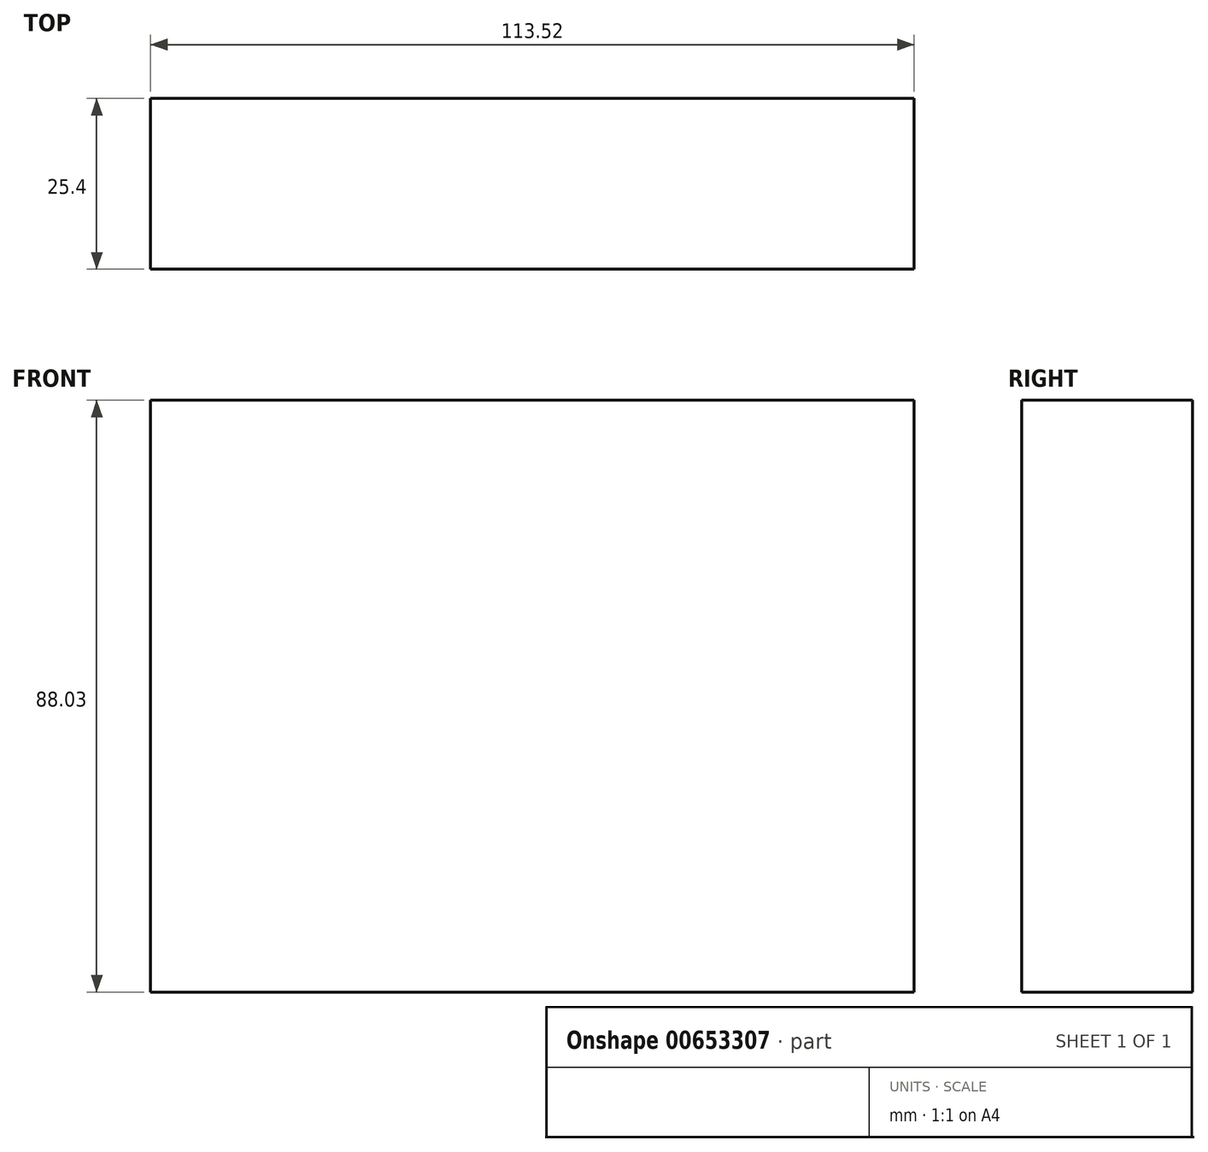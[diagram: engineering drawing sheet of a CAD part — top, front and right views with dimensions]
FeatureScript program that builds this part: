
annotation { "Feature Type Name" : "Feature", "Feature Type Description" : "" }
export const myFeature = defineFeature(function(context is Context, id is Id, definition is map)
    precondition{}
    {
        {
            var Q0;
            Q0=qCreatedBy(makeId("Front.planeOp"),FACE);
            var sketch = newSketch(context, id + "F0", { "sketchPlane" : qUnion([Q0])});
            skLineSegment(sketch, "E0.bottom", {"start": v(-50.13, 54) * mm, "end": v(63.4, 54) * mm});
            skLineSegment(sketch, "E0.top", {"start": v(-50.13, -34.04) * mm, "end": v(63.4, -34.04) * mm});
            skLineSegment(sketch, "E0.left", {"start": v(-50.13, 54) * mm, "end": v(-50.13, -34.04) * mm});
            skLineSegment(sketch, "E0.right", {"start": v(63.4, 54) * mm, "end": v(63.4, -34.04) * mm});
            skSolve(sketch);
        }
        {
            var Q0;
            Q0=makeQuery(id+"F0.imprint","IMPRINT",FACE,{"disambiguationData":[TD([[makeQuery(id+"F0.imprint","IMPRINT",EDGE,{"derivedFrom":sQuery(id+"F0.wireOp",EDGE,"E0.bottom")}),-1.0]])]});
            extrude(context, id + "F1", {"entities" : qUnion([Q0]), "depth" : 25.4 * mm, "offsetDistance" : 25.4 * mm});
        }
    });
